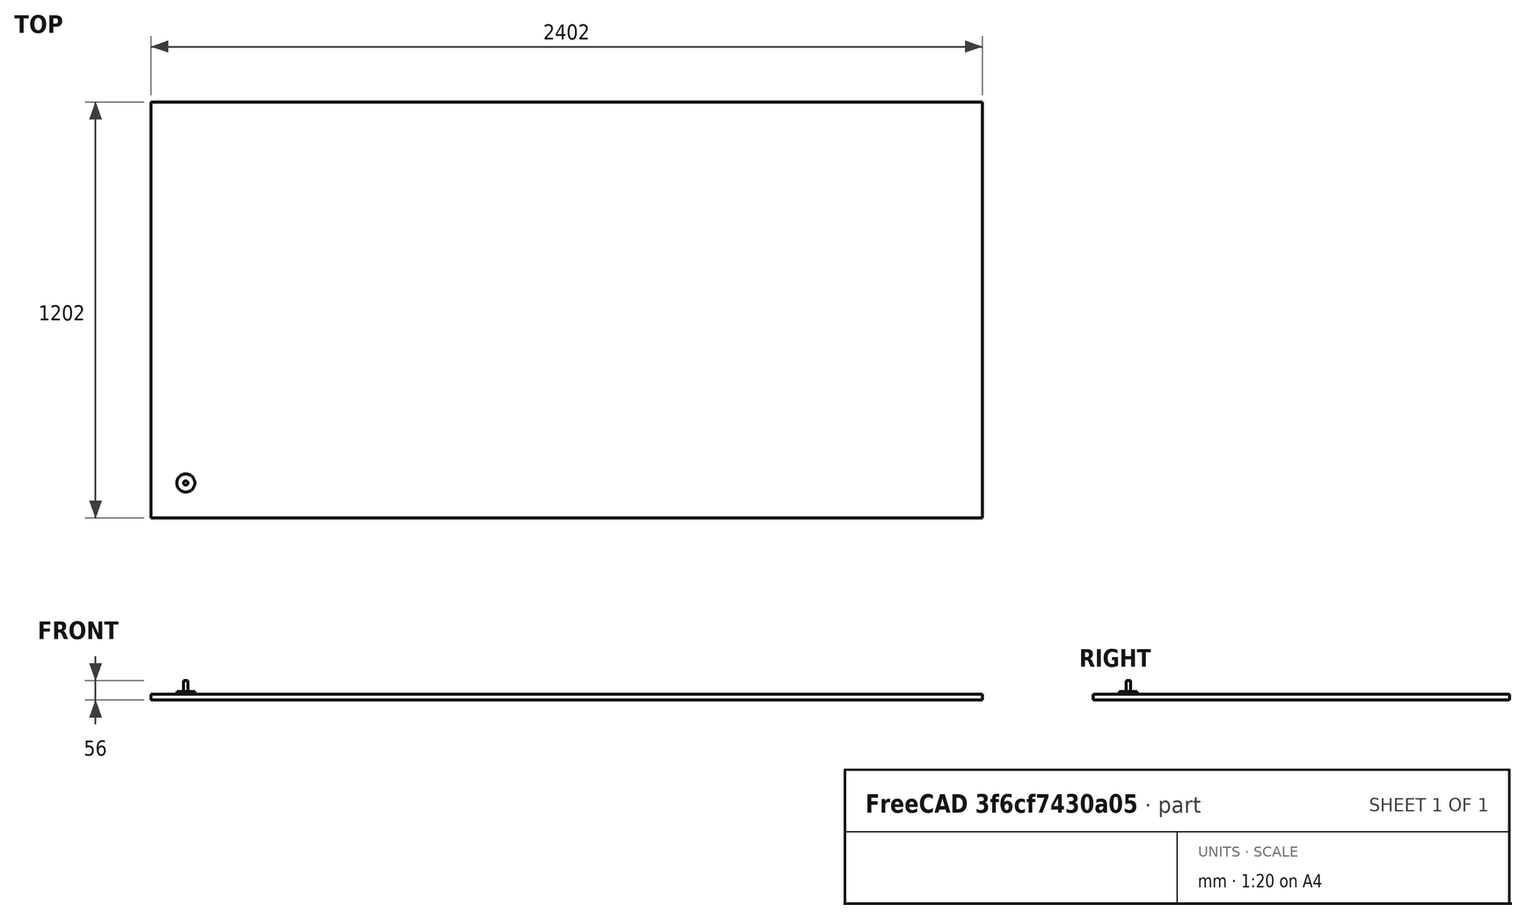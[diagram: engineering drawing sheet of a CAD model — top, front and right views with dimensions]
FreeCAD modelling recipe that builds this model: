
FCSTD DOCUMENT  (FreeCAD 0.19R14555 (Git shallow))
Label: SkimTable
License: All rights reserved
LicenseURL: http://en.wikipedia.org/wiki/All_rights_reserved
objects: Part::FeaturePython×3, Path::FeaturePython×3, App::DocumentObjectGroup×2, Sketcher::SketchObject×1, PartDesign::Pad×1, PartDesign::Body×1, App::FeaturePython×1, Path::FeatureCompoundPython×1, Mesh::FeaturePython×1
note: 8 computed .brp shape members not serialized (recipe doc carries the construction recipe); baked Part::Feature solids carry a one-line shape summary decoded from their .brp

FEATURE [Sketcher::SketchObject] Sketch
  FullyConstrained = true
  MapMode = 5
  Support = -> [XY_Plane]
  sketch-geometry (4):
    g0: LineSegment StartX=-100 StartY=1100 StartZ=0 EndX=2300 EndY=1100 EndZ=0
    g1: LineSegment StartX=2300 StartY=1100 StartZ=0 EndX=2300 EndY=-100 EndZ=0
    g2: LineSegment StartX=2300 StartY=-100 StartZ=0 EndX=-100 EndY=-100 EndZ=0
    g3: LineSegment StartX=-100 StartY=-100 StartZ=0 EndX=-100 EndY=1100 EndZ=0
  constraints (12):
    c: Coincident(g0,g1)
    c: Coincident(g1,g2)
    c: Coincident(g2,g3)
    c: Coincident(g3,g0)
    c: Horizontal(g0)
    c: Horizontal(g2)
    c: Vertical(g1)
    c: Vertical(g3)
    c: DistanceX(g2,g-1) = 100
    c: DistanceY(g2,g-1) = 100
    c: DistanceX(g0,g0) = 2400
    c: DistanceY(g3,g3) = 1200
FEATURE [PartDesign::Pad] Pad
  Direction = (1,1,1)
  Length = 15
  Length2 = 100
  Profile = -> Sketch
  Reversed = true
  Type = 0
FEATURE [PartDesign::Body] Body  label="Table"
  Group = -> [Sketch,Pad]
  Origin = -> Origin
  Tip = -> Pad
FEATURE [App::FeaturePython] SetupSheet  # Path/CAM operation (typed FeaturePython)
  ClearanceHeightExpression = OpStockZMax+SetupSheet.ClearanceHeightOffset
  ClearanceHeightOffset = 5
  CoolantMode = 0
  CoolantModes = None | Flood | Mist
  FinalDepthExpression = OpFinalDepth
  HorizRapid = 0
  SafeHeightExpression = OpStockZMax+SetupSheet.SafeHeightOffset
  SafeHeightOffset = 3
  StartDepthExpression = OpStartDepth
  StepDownExpression = OpToolDiameter
  VertRapid = 0
FEATURE [Part::FeaturePython] Clone  label="Model-Table"  # Draft clone (typed FeaturePython)
  AttacherType = Attacher::AttachEngine3D
  Fuse = false
  Objects = -> [Body]
  PathResource = Model
  Scale = (1,1,1)
FEATURE [App::DocumentObjectGroup] Model
  Group = -> [Clone]
FEATURE [Part::FeaturePython] Stock  # WARN: FeaturePython — macro-defined, semantics opaque (R4)
  Base = -> Model
  ExtXneg = 1
  ExtXpos = 1
  ExtYneg = 1
  ExtYpos = 1
  ExtZneg = 1
  ExtZpos = 1
  Placement = pos=(-100,-100,-15) rot=(0,0,1;0rad)
  StockType = FromBase
FEATURE [Part::FeaturePython] ToolBit001  label="52mm Endmill"  # Path/CAM toolbit (typed FeaturePython)
  BitPropertyNames = Chipload | CuttingEdgeHeight | Diameter | Flutes | Length | Material | ShankDiameter
  BitShape = /app/freecad/Mod/Path/Tools/Shape/endmill.fcstd
  Chipload = 0
  CuttingEdgeHeight = 9
  Diameter = 52
  File = <userpath>/Documents/MensShed/FreeCAD/Bit/52mm_EndMill.fctb
  Flutes = 0
  Length = 40
  Material = 0
  ShankDiameter = 12.7
  ShapeName = endmill
FEATURE [Path::FeaturePython] _2mm_Endmill  label="52mm Endmill001"  # Path/CAM operation (typed FeaturePython)
  HorizFeed = 40
  HorizRapid = 0
  SpindleDir = 0
  SpindleSpeed = 10000
  Tool = -> ToolBit001
  ToolNumber = 1
  VertFeed = 40
  VertRapid = 0
  expr: HorizRapid = SetupSheet.HorizRapid
  expr: VertRapid = SetupSheet.VertRapid
FEATURE [App::DocumentObjectGroup] Tools
  Group = -> [_2mm_Endmill]
FEATURE [Path::FeaturePython] MillFace  # Path/CAM operation (typed FeaturePython)
  Active = true
  AreaParams:
    Tolerance = 1e-07
    FitArcs = True
    Simplify = False
    CleanDistance = 0.0
    Accuracy = 0.01
    Unit = 1.0
    MinArcPoints = 4
    MaxArcPoints = 100
    ClipperScale = 10000000.0
    Fill = 0
    Coplanar = 0
    Reorient = True
    Outline = False
    Explode = False
    OpenMode = 0
    Deflection = 0.01
    SubjectFill = 0
    ClipFill = 0
    Offset = 0.0
    ExtraPass = 0
    Stepover = 0.0
    LastStepover = 0.0
    JoinType = 0
    EndType = 0
    MiterLimit = 2.0
    RoundPrecision = 0.0
    PocketMode = 2
    ToolRadius = 26.0
    PocketExtraOffset = 0.0
    PocketStepover = 39.0
    PocketLastStepover = 0.0
    FromCenter = True
    Angle = 45.0
    AngleShift = 0.0
    Shift = 0.0
    Thicken = False
    SectionCount = -1
    Stepdown = 1.0
    SectionOffset = 0.0
    SectionTolerance = 1e-06
    SectionMode = 2
    Project = False
  Base = -> [Clone]
  BoundaryShape = 0
  ClearEdges = false
  ClearanceHeight = 6
  CoolantMode = None
  CutMode = 1
  CycleTime = 00:33:35
  EnableRotation = 0
  ExcludeRaisedAreas = false
  ExtraOffset = 0
  FinalDepth = -1
  FinishDepth = 1
  KeepToolDown = false
  MinTravel = false
  OffsetPattern = 1
  OpFinalDepth = 0
  OpStartDepth = 1
  OpStockZMax = 1
  OpStockZMin = -16
  OpToolDiameter = 52
  PathParams = {'orientation': 0, 'feedrate': 40.0, 'feedrate_v': 40.0, 'verbose': True, 'resume_height': 4.0, 'retraction': 6.0, 'return_end': True, 'preamble': False}
  SafeHeight = 4
  StartAt = 0
  StartDepth = 0
  StartPoint = (0,0,0)
  StepDown = 1
  StepOver = 75
  ToolController = -> _2mm_Endmill
  UseStartPoint = false
  ZigZagAngle = 45
  expr: FinishDepth = 1mm
  expr: ClearanceHeight = OpStockZMax + SetupSheet.ClearanceHeightOffset
  expr: SafeHeight = OpStockZMax + SetupSheet.SafeHeightOffset
  expr: StepDown = 1
  expr: FinalDepth = -1
  expr: StartDepth = 0
FEATURE [Path::FeatureCompoundPython] Operations  # Path/CAM operation (typed FeaturePython)
  Group = -> [MillFace]
  UsePlacements = false
FEATURE [Path::FeaturePython] Job  label="Skim 1mm"  # Path/CAM operation (typed FeaturePython)
  CycleTime = 00:33:35
  Fixtures = G54
  GeometryTolerance = 0.01
  LastPostProcessDate = 2021-12-09 15:48:39.044029
  LastPostProcessOutput = <userpath>/Documents/MensShed/SkimTable.ngc
  Model = -> Model
  Operations = -> Operations
  OrderOutputBy = 0
  PostProcessor = 7
  PostProcessorOutputFile = <userpath>/Documents/MensShed/SkimTable.ngc
  SetupSheet = -> SetupSheet
  SplitOutput = false
  Stock = -> Stock
  Tools = -> Tools
FEATURE [Mesh::FeaturePython] CutMaterial  # WARN: FeaturePython — macro-defined, semantics opaque (R4)
